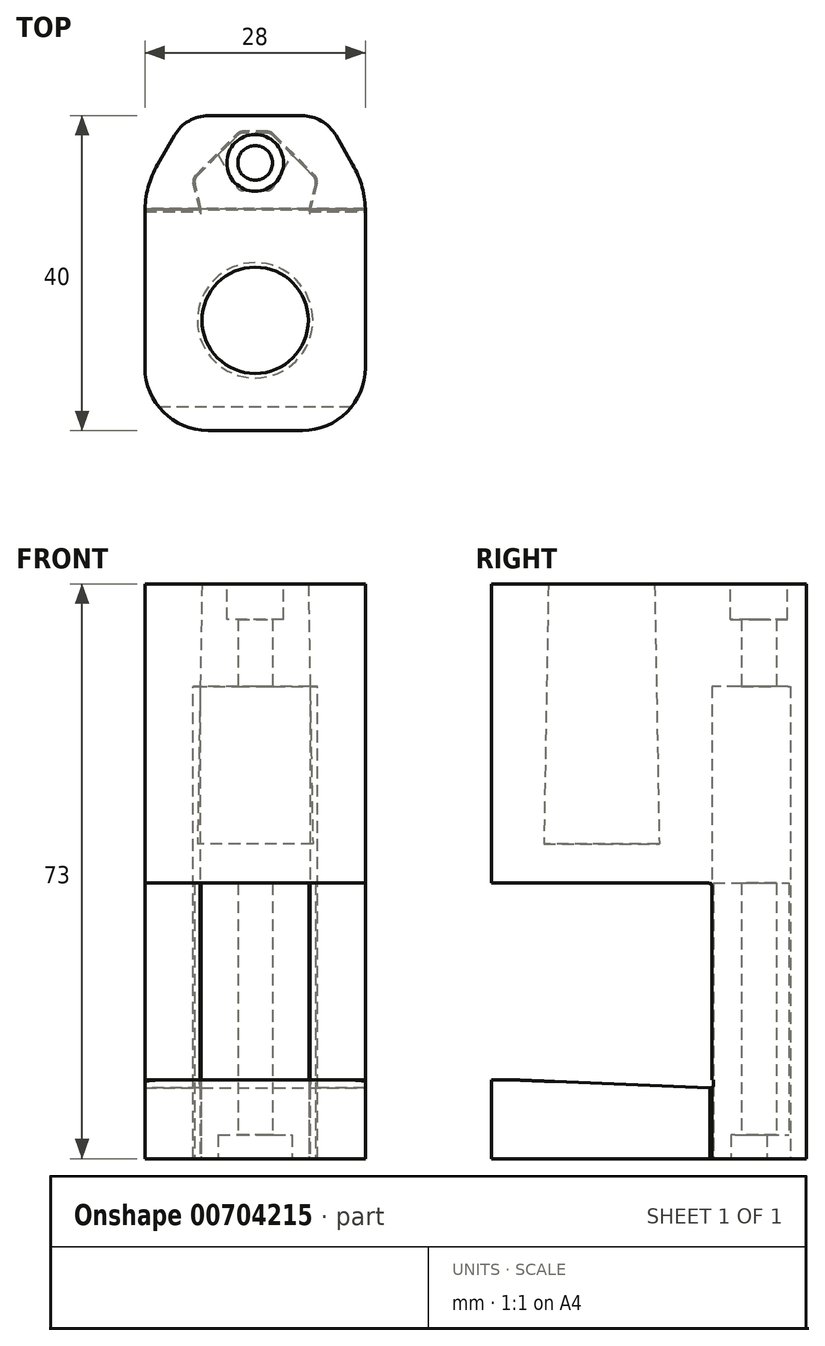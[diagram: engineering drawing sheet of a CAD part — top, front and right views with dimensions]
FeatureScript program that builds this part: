
annotation { "Feature Type Name" : "Feature", "Feature Type Description" : "" }
export const myFeature = defineFeature(function(context is Context, id is Id, definition is map)
    precondition{}
    {
        {
            assignVariable(context, id + "F0", {"name" : "lamppostDepth", "anyValue" : 33});
        }
        {
            var Q0;
            Q0=qCreatedBy(makeId("Right.planeOp"),FACE);
            var sketch = newSketch(context, id + "F1", { "sketchPlane" : qUnion([Q0])});
            skLineSegment(sketch, "E0", {"start": v(0, 0) * mm, "end": v(-28, 0) * mm});
            skLineSegment(sketch, "E1", {"start": v(-28, 0) * mm, "end": v(-28, 38) * mm});
            skLineSegment(sketch, "E2", {"start": v(-28, 38) * mm, "end": v(12, 38) * mm});
            skLineSegment(sketch, "E3", {"start": v(12, 38) * mm, "end": v(12, -35) * mm});
            skLineSegment(sketch, "E4", {"start": v(12, -35) * mm, "end": v(0, -35) * mm});
            skLineSegment(sketch, "E5", {"start": v(0, -35) * mm, "end": v(0, 0) * mm});
            skLineSegment(sketch, "E6", {"start": v(0, -25) * mm, "end": v(-22.92, -25) * mm, "construction": true});
            skSolve(sketch);
        }
        {
            var Q0;
            Q0 = qSketchRegion(id + "F1", true);
            extrude(context, id + "F2", {"entities" : qUnion([Q0]), "endBound" : BoundingType.SYMMETRIC, "depth" : 28 * mm, "offsetDistance" : 25 * mm});
        }
        {
            var Q0;
            Q0=makeQuery(id+"F2.opExtrude","SWEPT_FACE",FACE,{"disambiguationData":[OSD([sQuery(id+"F1.wireOp",EDGE,"E2")])]});
            var sketch = newSketch(context, id + "F3", { "sketchPlane" : qUnion([Q0])});
            skCircle(sketch, "E7", {"center": v(0, -14) * mm, "radius": 6.75 * mm});
            skLineSegment(sketch, "E8", {"start": v(14, -28) * mm, "end": v(-14, 0) * mm, "construction": true});
            skLineSegment(sketch, "E9", {"start": v(-14, 0) * mm, "end": v(-14, -28) * mm, "construction": true});
            skSolve(sketch);
        }
        {
            var Q0;
            Q0 = qSketchRegion(id + "F3", true);
            extrude(context, id + "F4", {"entities" : qUnion([Q0]), "operationType" : NewBodyOperationType.REMOVE, "oppositeDirection" : true, "depth" : (getVariable(context, 'lamppostDepth')) * mm, "offsetDistance" : 25 * mm, "hasDraft" : true, "draftAngle" : 1 * degree});
        }
        {
            var Q0;
            Q0=makeQuery(id+"F2.opExtrude","SWEPT_FACE",FACE,{"disambiguationData":[OSD([sQuery(id+"F1.wireOp",EDGE,"E4")])]});
            var sketch = newSketch(context, id + "F5", { "sketchPlane" : qUnion([Q0])});
            skCircle(sketch, "E10", {"center": v(0, -6) * mm, "radius": 2.2 * mm});
            skLineSegment(sketch, "E11", {"start": v(-14, -12) * mm, "end": v(14, 0) * mm, "construction": true});
            skSolve(sketch);
        }
        {
            var Q0;
            Q0 = qSketchRegion(id + "F5", true);
            extrude(context, id + "F6", {"entities" : qUnion([Q0]), "operationType" : NewBodyOperationType.REMOVE, "endBound" : BoundingType.THROUGH_ALL, "oppositeDirection" : true, "depth" : 25 * mm, "offsetDistance" : 25 * mm});
        }
        {
            var Q0;
            Q0=makeQuery(id+"F2.opExtrude","SWEPT_FACE",FACE,{"disambiguationData":[OSD([sQuery(id+"F1.wireOp",EDGE,"E2")])]});
            var sketch = newSketch(context, id + "F7", { "sketchPlane" : qUnion([Q0])});
            skCircle(sketch, "E12", {"center": v(0, 6) * mm, "radius": 3.6 * mm});
            skSolve(sketch);
        }
        {
            var Q0;
            Q0 = qSketchRegion(id + "F7", true);
            extrude(context, id + "F8", {"entities" : qUnion([Q0]), "operationType" : NewBodyOperationType.REMOVE, "oppositeDirection" : true, "depth" : 4.5 * mm, "offsetDistance" : 25 * mm});
        }
        {
            var Q0;
            Q0=makeQuery(id+"F2.opExtrude","SWEPT_FACE",FACE,{"disambiguationData":[OSD([sQuery(id+"F1.wireOp",EDGE,"E4")])]});
            var sketch = newSketch(context, id + "F9", { "sketchPlane" : qUnion([Q0])});
            skLineSegment(sketch, "E13", {"start": v(2, -10) * mm, "end": v(-2, -10) * mm});
            skPoint(sketch, "E14", {"position": v(0, -6) * mm});
            skLineSegment(sketch, "E15", {"start": v(0, -6) * mm, "end": v(0, -10) * mm, "construction": true});
            skLineSegment(sketch, "E16", {"start": v(2, -10) * mm, "end": v(8, -4) * mm});
            skLineSegment(sketch, "E17", {"start": v(8, -4) * mm, "end": v(7, 0) * mm});
            skLineSegment(sketch, "E18", {"start": v(7, 0) * mm, "end": v(-7, 0) * mm});
            skLineSegment(sketch, "E19", {"start": v(-7, 0) * mm, "end": v(-8, -4) * mm});
            skLineSegment(sketch, "E20", {"start": v(-8, -4) * mm, "end": v(-2, -10) * mm});
            skSolve(sketch);
        }
        {
            var Q0;
            Q0 = qSketchRegion(id + "F9", true);
            extrude(context, id + "F10", {"entities" : qUnion([Q0]), "operationType" : NewBodyOperationType.REMOVE, "oppositeDirection" : true, "depth" : 60 * mm, "offsetDistance" : 25 * mm});
        }
        {
            var Q0;
            Q0=makeQuery(id+"F2.opExtrude","SWEPT_FACE",FACE,{"disambiguationData":[OSD([sQuery(id+"F1.wireOp",EDGE,"E4")])]});
            var sketch = newSketch(context, id + "F11", { "sketchPlane" : qUnion([Q0])});
            skLineSegment(sketch, "E21.0", {"start": v(7.78, -3.94) * mm, "end": v(6.84, -0.2) * mm});
            skLineSegment(sketch, "E21.1", {"start": v(-6.84, -0.2) * mm, "end": v(-7.78, -3.94) * mm});
            skLineSegment(sketch, "E21.2", {"start": v(-7.78, -3.94) * mm, "end": v(-1.92, -9.8) * mm});
            skLineSegment(sketch, "E21.3", {"start": v(1.92, -9.8) * mm, "end": v(-1.92, -9.8) * mm});
            skLineSegment(sketch, "E21.4", {"start": v(1.92, -9.8) * mm, "end": v(7.78, -3.94) * mm});
            skLineSegment(sketch, "E22", {"start": v(6.84, -0.2) * mm, "end": v(-6.84, -0.2) * mm});
            skCircle(sketch, "E23.0", {"center": v(0, -6) * mm, "radius": 2.2 * mm});
            skSolve(sketch);
        }
        {
            var Q0;
            Q0 = qSketchRegion(id + "F11", true);
            extrude(context, id + "F12", {"entities" : qUnion([Q0]), "oppositeDirection" : true, "depth" : 35 * mm, "offsetDistance" : 25 * mm});
        }
        {
            var Q0;
            Q0=makeQuery(id+"F12.opExtrude","CAP_FACE",FACE,{"disambiguationData":[OSD([sQuery(id+"F11.wireOp",EDGE,"E21.0"),sQuery(id+"F11.wireOp",EDGE,"E21.1"),sQuery(id+"F11.wireOp",EDGE,"E21.2"),sQuery(id+"F11.wireOp",EDGE,"E21.3"),sQuery(id+"F11.wireOp",EDGE,"E21.4"),sQuery(id+"F11.wireOp",EDGE,"E22"),sQuery(id+"F11.wireOp",EDGE,"E23.0")])],"isStart":true});
            var sketch = newSketch(context, id + "F13", { "sketchPlane" : qUnion([Q0])});
            skLineSegment(sketch, "E24", {"start": v(14, 28) * mm, "end": v(-14, 28) * mm});
            skLineSegment(sketch, "E25", {"start": v(-14, 28) * mm, "end": v(-14, 0.2) * mm});
            skLineSegment(sketch, "E26", {"start": v(-14, 0.2) * mm, "end": v(-6.84, 0.2) * mm});
            skLineSegment(sketch, "E27", {"start": v(-6.84, 0.2) * mm, "end": v(-6.84, -0.2) * mm});
            skLineSegment(sketch, "E28", {"start": v(-6.84, -0.2) * mm, "end": v(6.84, -0.2) * mm});
            skLineSegment(sketch, "E29", {"start": v(6.84, -0.2) * mm, "end": v(6.84, 0.2) * mm});
            skLineSegment(sketch, "E30", {"start": v(6.84, 0.2) * mm, "end": v(14, 0.2) * mm});
            skLineSegment(sketch, "E31", {"start": v(14, 0.2) * mm, "end": v(14, 28) * mm});
            skSolve(sketch);
        }
        {
            var Q0;
            Q0=makeQuery(id+"F13.imprint","IMPRINT",FACE,{"disambiguationData":[TD([[makeQuery(id+"F13.imprint","IMPRINT",EDGE,{"derivedFrom":sQuery(id+"F13.wireOp",EDGE,"E24")}),1.0]])]});
            var Q1;
            Q1=sQuery(id+"F1.wireOp",VERTEX,"E6.end");
            extrude(context, id + "F14", {"entities" : qUnion([Q0]), "operationType" : NewBodyOperationType.ADD, "endBound" : BoundingType.UP_TO_VERTEX, "oppositeDirection" : true, "depth" : 10 * mm, "endBoundEntityVertex" : qUnion([Q1]), "offsetDistance" : 25 * mm});
        }
        {
            var Q0;
            Q0=makeQuery(id+"F14.boolean.opBoolean","MERGE",FACE,{"derivedFrom":[makeQuery(id+"F12.opExtrude","CAP_FACE",FACE,{"disambiguationData":[OSD([sQuery(id+"F11.wireOp",EDGE,"E21.0"),sQuery(id+"F11.wireOp",EDGE,"E21.1"),sQuery(id+"F11.wireOp",EDGE,"E21.2"),sQuery(id+"F11.wireOp",EDGE,"E21.3"),sQuery(id+"F11.wireOp",EDGE,"E21.4"),sQuery(id+"F11.wireOp",EDGE,"E22"),sQuery(id+"F11.wireOp",EDGE,"E23.0")])],"isStart":true}),makeQuery(id+"F14.opExtrude","CAP_FACE",FACE,{"disambiguationData":[OSD([sQuery(id+"F13.wireOp",EDGE,"E24"),sQuery(id+"F13.wireOp",EDGE,"E25"),sQuery(id+"F13.wireOp",EDGE,"E26"),sQuery(id+"F13.wireOp",EDGE,"E27"),sQuery(id+"F13.wireOp",EDGE,"E28"),sQuery(id+"F13.wireOp",EDGE,"E29"),sQuery(id+"F13.wireOp",EDGE,"E30"),sQuery(id+"F13.wireOp",EDGE,"E31")])],"isStart":true})]});
            var sketch = newSketch(context, id + "F15", { "sketchPlane" : qUnion([Q0])});
            skCircle(sketch, "E32", {"center": v(0, -6) * mm, "radius": 4.1 * mm, "construction": true});
            skLineSegment(sketch, "E33", {"start": v(2.05, -2.45) * mm, "end": v(-2.05, -2.45) * mm});
            skLineSegment(sketch, "E34", {"start": v(2.05, -2.45) * mm, "end": v(4.1, -6) * mm});
            skLineSegment(sketch, "E35", {"start": v(4.1, -6) * mm, "end": v(0, -6) * mm, "construction": true});
            skLineSegment(sketch, "E36", {"start": v(0, -6) * mm, "end": v(-4.1, -6) * mm, "construction": true});
            skLineSegment(sketch, "E37", {"start": v(-4.1, -6) * mm, "end": v(-2.05, -2.45) * mm});
            skLineSegment(sketch, "E38", {"start": v(4.1, -6) * mm, "end": v(4.7, -7.03) * mm});
            skLineSegment(sketch, "E39", {"start": v(4.7, -7.03) * mm, "end": v(1.92, -9.8) * mm});
            skLineSegment(sketch, "E40", {"start": v(1.92, -9.8) * mm, "end": v(-1.92, -9.8) * mm});
            skLineSegment(sketch, "E41", {"start": v(-1.92, -9.8) * mm, "end": v(-4.7, -7.03) * mm});
            skLineSegment(sketch, "E42", {"start": v(-4.7, -7.03) * mm, "end": v(-4.1, -6) * mm});
            skSolve(sketch);
        }
        {
            var Q0;
            Q0 = qSketchRegion(id + "F15", true);
            extrude(context, id + "F16", {"entities" : qUnion([Q0]), "operationType" : NewBodyOperationType.REMOVE, "oppositeDirection" : true, "depth" : 3 * mm, "offsetDistance" : 25 * mm});
        }
        {
            var Q0;
            Q0=makeQuery(id+"F2.opExtrude","CAP_EDGE",EDGE,{"disambiguationData":[OSD([sQuery(id+"F1.wireOp",EDGE,"E1")])],"isStart":false});
            var Q1;
            Q1=makeQuery(id+"F2.opExtrude","CAP_EDGE",EDGE,{"disambiguationData":[OSD([sQuery(id+"F1.wireOp",EDGE,"E1")])],"isStart":true});
            var Q2;
            Q2=makeQuery(id+"F14.opExtrude","SWEPT_EDGE",EDGE,{"disambiguationData":[OSD([sQuery(id+"F13.wireOp",EDGE,"E24"),sQuery(id+"F13.wireOp",EDGE,"E31")])]});
            var Q3;
            Q3=makeQuery(id+"F14.opExtrude","SWEPT_EDGE",EDGE,{"disambiguationData":[OSD([sQuery(id+"F13.wireOp",EDGE,"E24"),sQuery(id+"F13.wireOp",EDGE,"E25")])]});
            fillet(context, id + "F17", {"entities" : qUnion([Q0, Q1, Q2, Q3]), "radius" : 8 * mm, "tangentPropagation" : true, "allowEdgeOverflow" : false});
        }
        {
            var Q0;
            Q0=makeQuery(id+"F2.opExtrude","CAP_EDGE",EDGE,{"disambiguationData":[OSD([sQuery(id+"F1.wireOp",EDGE,"E3")])],"isStart":true});
            var Q1;
            Q1=makeQuery(id+"F2.opExtrude","CAP_EDGE",EDGE,{"disambiguationData":[OSD([sQuery(id+"F1.wireOp",EDGE,"E3")])],"isStart":false});
            chamfer(context, id + "F18", {"entities" : qUnion([Q0, Q1]), "chamferType" : ChamferType.OFFSET_ANGLE, "width" : 9 * mm, "oppositeDirection" : false, "angle" : 30 * degree, "tangentPropagation" : true});
        }
        {
            var Q0;
            {var subQ0=sQuery(id+"F1.wireOp",EDGE,"E3");Q0=makeQuery(id+"F18.opChamfer","BLEND_EDGE",EDGE,{"blendedFrom":[makeQuery(id+"F2.opExtrude","CAP_EDGE",EDGE,{"disambiguationData":[OSD([subQ0])],"isStart":true}),makeQuery(id+"F2.opExtrude","CAP_FACE",FACE,{"disambiguationData":[OSD([sQuery(id+"F1.wireOp",EDGE,"E0"),sQuery(id+"F1.wireOp",EDGE,"E1"),sQuery(id+"F1.wireOp",EDGE,"E2"),subQ0,sQuery(id+"F1.wireOp",EDGE,"E4"),sQuery(id+"F1.wireOp",EDGE,"E5")])],"isStart":true})],"blendedInto":[makeQuery(id+"F2.opExtrude","CAP_FACE",FACE,{"disambiguationData":[OSD([sQuery(id+"F1.wireOp",EDGE,"E0"),sQuery(id+"F1.wireOp",EDGE,"E1"),sQuery(id+"F1.wireOp",EDGE,"E2"),subQ0,sQuery(id+"F1.wireOp",EDGE,"E4"),sQuery(id+"F1.wireOp",EDGE,"E5")])],"isStart":true})]});}
            var Q1;
            {var subQ0=sQuery(id+"F1.wireOp",EDGE,"E3");Q1=makeQuery(id+"F18.opChamfer","BLEND_EDGE",EDGE,{"blendedFrom":[makeQuery(id+"F2.opExtrude","CAP_EDGE",EDGE,{"disambiguationData":[OSD([subQ0])],"isStart":false}),makeQuery(id+"F2.opExtrude","CAP_FACE",FACE,{"disambiguationData":[OSD([sQuery(id+"F1.wireOp",EDGE,"E0"),sQuery(id+"F1.wireOp",EDGE,"E1"),sQuery(id+"F1.wireOp",EDGE,"E2"),subQ0,sQuery(id+"F1.wireOp",EDGE,"E4"),sQuery(id+"F1.wireOp",EDGE,"E5")])],"isStart":false})],"blendedInto":[makeQuery(id+"F2.opExtrude","CAP_FACE",FACE,{"disambiguationData":[OSD([sQuery(id+"F1.wireOp",EDGE,"E0"),sQuery(id+"F1.wireOp",EDGE,"E1"),sQuery(id+"F1.wireOp",EDGE,"E2"),subQ0,sQuery(id+"F1.wireOp",EDGE,"E4"),sQuery(id+"F1.wireOp",EDGE,"E5")])],"isStart":false})]});}
            fillet(context, id + "F19", {"entities" : qUnion([Q0, Q1]), "radius" : 12 * mm, "tangentPropagation" : true, "allowEdgeOverflow" : false});
        }
        {
            var Q0;
            {var subQ0=sQuery(id+"F1.wireOp",EDGE,"E3");Q0=makeQuery(id+"F18.opChamfer","BLEND_EDGE",EDGE,{"blendedFrom":[makeQuery(id+"F2.opExtrude","CAP_EDGE",EDGE,{"disambiguationData":[OSD([subQ0])],"isStart":true}),makeQuery(id+"F2.opExtrude","SWEPT_FACE",FACE,{"disambiguationData":[OSD([subQ0])]})],"blendedInto":[makeQuery(id+"F2.opExtrude","SWEPT_FACE",FACE,{"disambiguationData":[OSD([subQ0])]})]});}
            var Q1;
            {var subQ0=sQuery(id+"F1.wireOp",EDGE,"E3");Q1=makeQuery(id+"F18.opChamfer","BLEND_EDGE",EDGE,{"blendedFrom":[makeQuery(id+"F2.opExtrude","CAP_EDGE",EDGE,{"disambiguationData":[OSD([subQ0])],"isStart":false}),makeQuery(id+"F2.opExtrude","SWEPT_FACE",FACE,{"disambiguationData":[OSD([subQ0])]})],"blendedInto":[makeQuery(id+"F2.opExtrude","SWEPT_FACE",FACE,{"disambiguationData":[OSD([subQ0])]})]});}
            fillet(context, id + "F20", {"entities" : qUnion([Q0, Q1]), "radius" : 5 * mm, "tangentPropagation" : true, "allowEdgeOverflow" : false});
        }
        {
            var Q0;
            Q0=makeQuery(id+"F14.opExtrude","SWEPT_FACE",FACE,{"disambiguationData":[OSD([sQuery(id+"F13.wireOp",EDGE,"E25")])]});
            var sketch = newSketch(context, id + "F21", { "sketchPlane" : qUnion([Q0])});
            skLineSegment(sketch, "E43", {"start": v(-0.2, -25) * mm, "end": v(25, -25) * mm});
            skLineSegment(sketch, "E44", {"start": v(25, -25) * mm, "end": v(-0.2, -26) * mm});
            skLineSegment(sketch, "E45", {"start": v(-0.2, -26) * mm, "end": v(-0.2, -25) * mm});
            skSolve(sketch);
        }
        {
            var Q0;
            Q0 = qSketchRegion(id + "F21", true);
            extrude(context, id + "F22", {"entities" : qUnion([Q0]), "operationType" : NewBodyOperationType.REMOVE, "endBound" : BoundingType.THROUGH_ALL, "oppositeDirection" : true, "depth" : 25 * mm, "offsetDistance" : 25 * mm});
        }
        {
            var Q0;
            Q0=makeQuery(id+"F14.opExtrude","CAP_EDGE",EDGE,{"disambiguationData":[OSD([sQuery(id+"F13.wireOp",EDGE,"E28")])],"isStart":false});
            var Q1;
            {var subQ0=sQuery(id+"F1.wireOp",EDGE,"E5");var subQ1=makeQuery(id+"F2.opExtrude","SWEPT_FACE",FACE,{"disambiguationData":[OSD([subQ0])]});var subQ2=sQuery(id+"F1.wireOp",EDGE,"E0");var subQ3=makeQuery(id+"F2.opExtrude","SWEPT_FACE",FACE,{"disambiguationData":[OSD([subQ2])]});Q1=makeQuery(id+"F10.boolean.opBoolean","SPLIT",EDGE,{"disambiguationData":[topologyDisambiguationEdgeConnected([subQ3,subQ1]),TD([makeQuery(id+"F10.opExtrude","SWEPT_FACE",FACE,{"disambiguationData":[OSD([sQuery(id+"F9.wireOp",EDGE,"E17")])]})])],"derivedFrom":makeQuery(id+"F2.opExtrude","SWEPT_EDGE",EDGE,{"disambiguationData":[OSD([subQ2,subQ0])]})});}
            var Q2;
            {var subQ0=sQuery(id+"F1.wireOp",EDGE,"E5");var subQ1=makeQuery(id+"F2.opExtrude","SWEPT_FACE",FACE,{"disambiguationData":[OSD([subQ0])]});var subQ2=sQuery(id+"F1.wireOp",EDGE,"E0");var subQ3=makeQuery(id+"F2.opExtrude","SWEPT_FACE",FACE,{"disambiguationData":[OSD([subQ2])]});Q2=makeQuery(id+"F10.boolean.opBoolean","SPLIT",EDGE,{"disambiguationData":[topologyDisambiguationEdgeConnected([subQ3,subQ1]),TD([makeQuery(id+"F10.opExtrude","SWEPT_FACE",FACE,{"disambiguationData":[OSD([sQuery(id+"F9.wireOp",EDGE,"E19")])]})])],"derivedFrom":makeQuery(id+"F2.opExtrude","SWEPT_EDGE",EDGE,{"disambiguationData":[OSD([subQ2,subQ0])]})});}
            var Q3;
            Q3=makeQuery(id+"F22.boolean.opBoolean","COPY",EDGE,{"derivedFrom":makeQuery(id+"F22.opExtrude","SWEPT_EDGE",EDGE,{"disambiguationData":[OSD([sQuery(id+"F21.wireOp",EDGE,"E44"),sQuery(id+"F21.wireOp",EDGE,"E45")])]})});
            fillet(context, id + "F23", {"entities" : qUnion([Q0, Q1, Q2, Q3]), "radius" : .5 * mm, "tangentPropagation" : true, "rho" : .7, "crossSection" : FilletCrossSection.CONIC, "allowEdgeOverflow" : false});
        }
        {
            var Q0;
            Q0=makeQuery(id+"F10.boolean.opBoolean","COPY",EDGE,{"derivedFrom":makeQuery(id+"F10.opExtrude","SWEPT_EDGE",EDGE,{"disambiguationData":[OSD([sQuery(id+"F9.wireOp",EDGE,"E19"),sQuery(id+"F9.wireOp",EDGE,"E20")])]})});
            var Q1;
            Q1=makeQuery(id+"F12.opExtrude","SWEPT_EDGE",EDGE,{"disambiguationData":[OSD([sQuery(id+"F11.wireOp",EDGE,"E21.1"),sQuery(id+"F11.wireOp",EDGE,"E21.2")])]});
            var Q2;
            Q2=makeQuery(id+"F16.boolean.opBoolean","COPY",EDGE,{"derivedFrom":makeQuery(id+"F16.opExtrude","SWEPT_EDGE",EDGE,{"disambiguationData":[OSD([sQuery(id+"F15.wireOp",EDGE,"E33"),sQuery(id+"F15.wireOp",EDGE,"E37")])]})});
            var Q3;
            Q3=makeQuery(id+"F16.boolean.opBoolean","COPY",EDGE,{"derivedFrom":makeQuery(id+"F16.opExtrude","SWEPT_EDGE",EDGE,{"disambiguationData":[OSD([sQuery(id+"F15.wireOp",EDGE,"E33"),sQuery(id+"F15.wireOp",EDGE,"E34")])]})});
            var Q4;
            Q4=makeQuery(id+"F10.boolean.opBoolean","COPY",EDGE,{"derivedFrom":makeQuery(id+"F10.opExtrude","SWEPT_EDGE",EDGE,{"disambiguationData":[OSD([sQuery(id+"F9.wireOp",EDGE,"E13"),sQuery(id+"F9.wireOp",EDGE,"E20")])]})});
            var Q5;
            Q5=makeQuery(id+"F10.boolean.opBoolean","COPY",EDGE,{"derivedFrom":makeQuery(id+"F10.opExtrude","SWEPT_EDGE",EDGE,{"disambiguationData":[OSD([sQuery(id+"F9.wireOp",EDGE,"E13"),sQuery(id+"F9.wireOp",EDGE,"E16")])]})});
            var Q6;
            Q6=makeQuery(id+"F10.boolean.opBoolean","COPY",EDGE,{"derivedFrom":makeQuery(id+"F10.opExtrude","SWEPT_EDGE",EDGE,{"disambiguationData":[OSD([sQuery(id+"F9.wireOp",EDGE,"E16"),sQuery(id+"F9.wireOp",EDGE,"E17")])]})});
            var Q7;
            Q7=makeQuery(id+"F12.opExtrude","SWEPT_EDGE",EDGE,{"disambiguationData":[OSD([sQuery(id+"F11.wireOp",EDGE,"E21.0"),sQuery(id+"F11.wireOp",EDGE,"E21.4")])]});
            var Q8;
            Q8=makeQuery(id+"F12.opExtrude","SWEPT_EDGE",EDGE,{"disambiguationData":[OSD([sQuery(id+"F11.wireOp",EDGE,"E21.3"),sQuery(id+"F11.wireOp",EDGE,"E21.4")])]});
            var Q9;
            Q9=makeQuery(id+"F12.opExtrude","SWEPT_EDGE",EDGE,{"disambiguationData":[OSD([sQuery(id+"F11.wireOp",EDGE,"E21.2"),sQuery(id+"F11.wireOp",EDGE,"E21.3")])]});
            fillet(context, id + "F24", {"entities" : qUnion([Q0, Q1, Q2, Q3, Q4, Q5, Q6, Q7, Q8, Q9]), "radius" : 1 * mm, "tangentPropagation" : true, "allowEdgeOverflow" : false});
        }
    });
